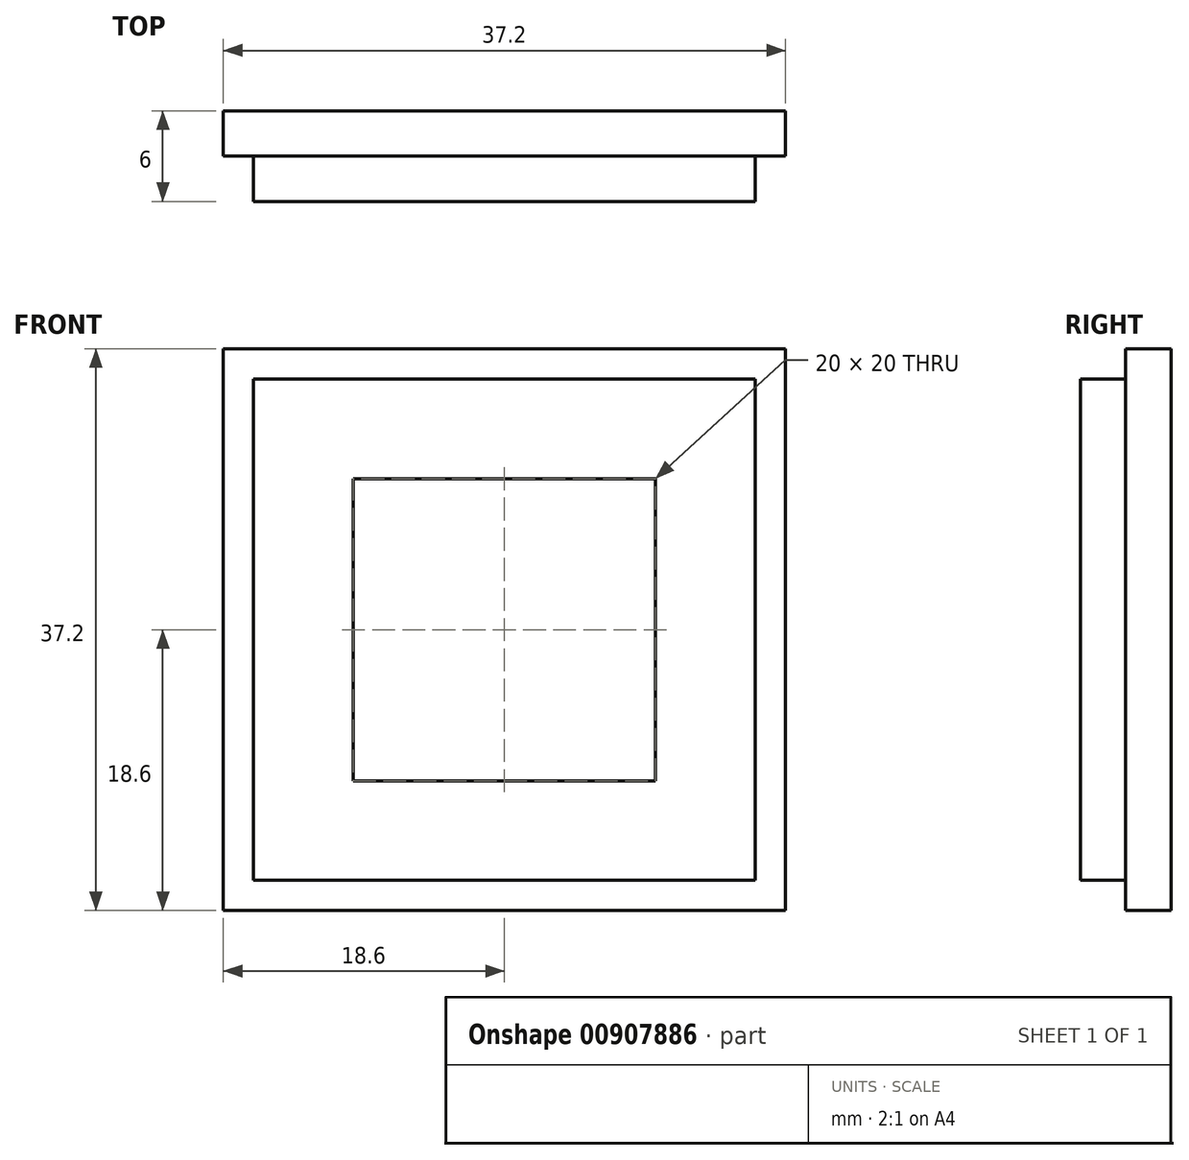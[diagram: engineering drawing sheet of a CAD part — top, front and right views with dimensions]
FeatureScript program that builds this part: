
annotation { "Feature Type Name" : "Feature", "Feature Type Description" : "" }
export const myFeature = defineFeature(function(context is Context, id is Id, definition is map)
    precondition{}
    {
        {
            var Q0;
            Q0=qCreatedBy(makeId("Front.planeOp"),FACE);
            var sketch = newSketch(context, id + "F0", { "sketchPlane" : qUnion([Q0])});
            skLineSegment(sketch, "E0.bottom", {"start": v(16.6, 16.6) * mm, "end": v(-16.6, 16.6) * mm});
            skLineSegment(sketch, "E0.top", {"start": v(16.6, -16.6) * mm, "end": v(-16.6, -16.6) * mm});
            skLineSegment(sketch, "E0.left", {"start": v(16.6, 16.6) * mm, "end": v(16.6, -16.6) * mm});
            skLineSegment(sketch, "E0.right", {"start": v(-16.6, 16.6) * mm, "end": v(-16.6, -16.6) * mm});
            skPoint(sketch, "E0.middle", {"position": v(0, 0) * mm});
            skLineSegment(sketch, "E1.0", {"start": v(18.6, 18.6) * mm, "end": v(-18.6, 18.6) * mm});
            skLineSegment(sketch, "E1.1", {"start": v(18.6, 18.6) * mm, "end": v(18.6, -18.6) * mm});
            skLineSegment(sketch, "E1.2", {"start": v(18.6, -18.6) * mm, "end": v(-18.6, -18.6) * mm});
            skLineSegment(sketch, "E1.3", {"start": v(-18.6, 18.6) * mm, "end": v(-18.6, -18.6) * mm});
            skLineSegment(sketch, "E2.bottom", {"start": v(10, 10) * mm, "end": v(-10, 10) * mm});
            skLineSegment(sketch, "E2.top", {"start": v(10, -10) * mm, "end": v(-10, -10) * mm});
            skLineSegment(sketch, "E2.left", {"start": v(10, 10) * mm, "end": v(10, -10) * mm});
            skLineSegment(sketch, "E2.right", {"start": v(-10, 10) * mm, "end": v(-10, -10) * mm});
            skSolve(sketch);
        }
        {
            var Q0;
            Q0=makeQuery(id+"F0.imprint","IMPRINT",FACE,{"disambiguationData":[TD([[makeQuery(id+"F0.imprint","IMPRINT",EDGE,{"derivedFrom":sQuery(id+"F0.wireOp",EDGE,"E0.bottom")}),-1.0]])]});
            extrude(context, id + "F1", {"entities" : qUnion([Q0]), "depth" : 3 * mm, "offsetDistance" : 25 * mm});
        }
        {
            var Q0;
            Q0=makeQuery(id+"F0.imprint","IMPRINT",FACE,{"disambiguationData":[TD([[makeQuery(id+"F0.imprint","IMPRINT",EDGE,{"derivedFrom":sQuery(id+"F0.wireOp",EDGE,"E0.bottom")}),1.0]])]});
            extrude(context, id + "F2", {"entities" : qUnion([Q0]), "operationType" : NewBodyOperationType.ADD, "depth" : 6 * mm, "offsetDistance" : 25 * mm});
        }
    });
